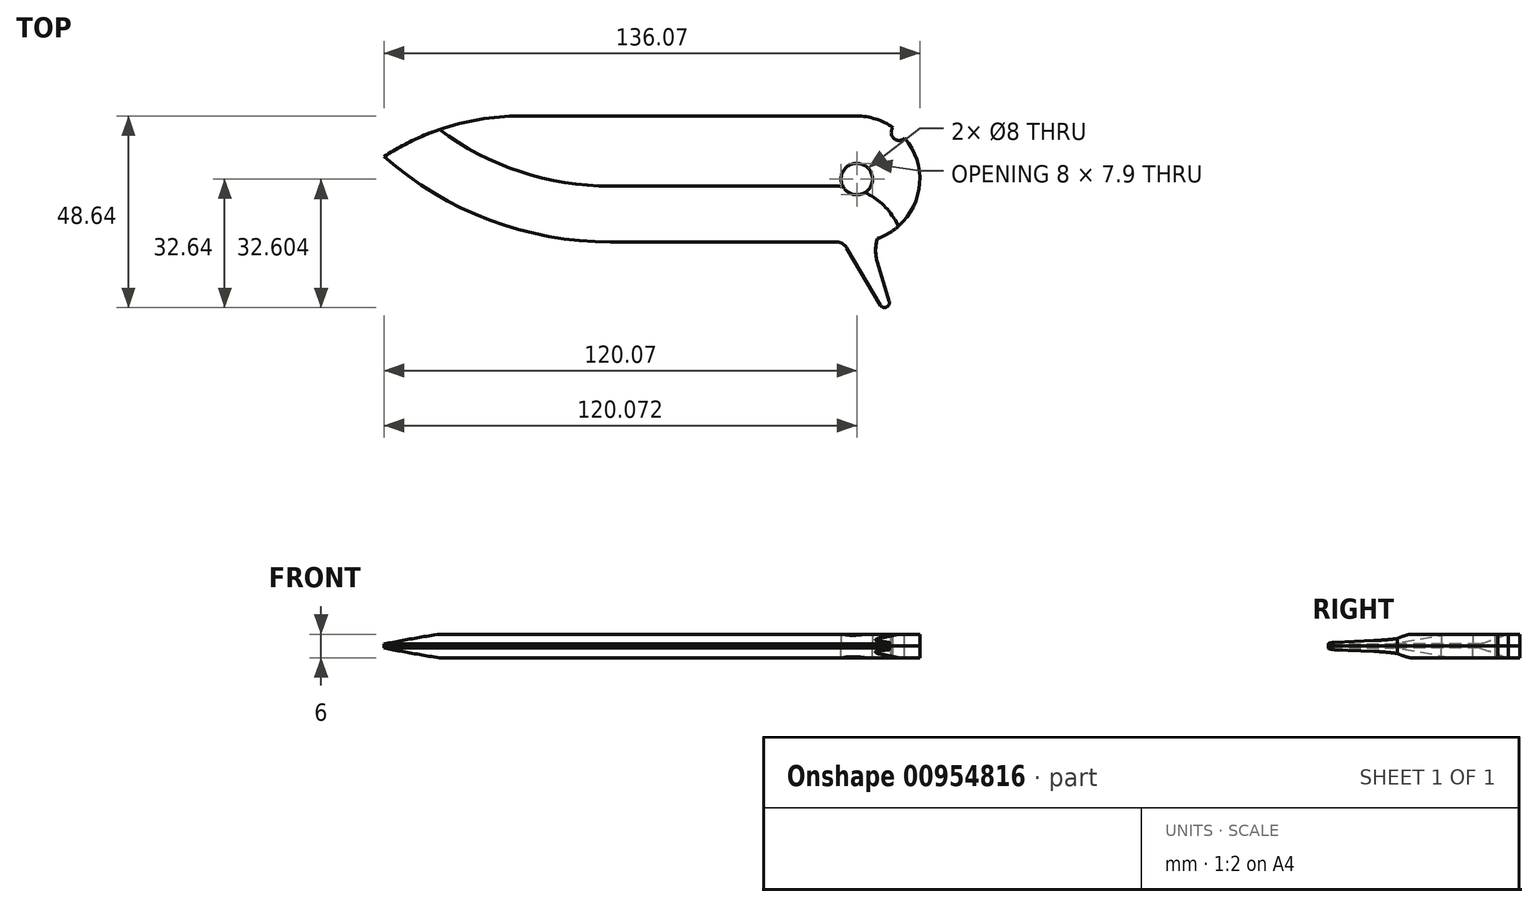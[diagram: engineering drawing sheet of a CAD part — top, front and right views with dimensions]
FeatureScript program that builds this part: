
annotation { "Feature Type Name" : "Feature", "Feature Type Description" : "" }
export const myFeature = defineFeature(function(context is Context, id is Id, definition is map)
    precondition{}
    {
        {
            var Q0;
            Q0=qCreatedBy(makeId("Top.planeOp"),FACE);
            var sketch = newSketch(context, id + "F0", { "sketchPlane" : qUnion([Q0])});
            skCircle(sketch, "E0", {"center": v(0, 0) * mm, "radius": 4 * mm});
            skArc(sketch, "E1", {"start": v(0, 16) * mm, "mid": v(15.78, 2.65) * mm, "end": v(5.24, -15.12) * mm});
            skLineSegment(sketch, "E2", {"start": v(0, 16) * mm, "end": v(-85.55, 16) * mm});
            skLineSegment(sketch, "E3", {"start": v(-62.58, -16) * mm, "end": v(-5.16, -16) * mm});
            skLineSegment(sketch, "E4", {"start": v(5.24, -21.16) * mm, "end": v(8.23, -31.02) * mm});
            skArc(sketch, "E5", {"start": v(8.23, -31.02) * mm, "mid": v(7.56, -32.53) * mm, "end": v(5.97, -32.07) * mm});
            skLineSegment(sketch, "E6", {"start": v(5.97, -32.07) * mm, "end": v(-2.57, -17.48) * mm});
            skArc(sketch, "E7.filletArc", {"start": v(-2.57, -17.48) * mm, "mid": v(-3.67, -16.4) * mm, "end": v(-5.16, -16) * mm});
            skArc(sketch, "E8", {"start": v(-85.55, 16) * mm, "mid": v(-103.56, 13.37) * mm, "end": v(-120.07, 5.7) * mm});
            skArc(sketch, "E9", {"start": v(-120.07, 5.7) * mm, "mid": v(-93.3, -10.4) * mm, "end": v(-62.58, -16) * mm});
            skPoint(sketch, "E10.orphan", {"position": v(-120, -16) * mm});
            skArc(sketch, "E11", {"start": v(5.24, -15.12) * mm, "mid": v(4.79, -18.14) * mm, "end": v(5.24, -21.16) * mm});
            skPoint(sketch, "E12.orphan", {"position": v(0, -16) * mm});
            skSolve(sketch);
        }
        {
            var Q0;
            Q0=makeQuery(id+"F0.imprint","IMPRINT",FACE,{"disambiguationData":[TD([[makeQuery(id+"F0.imprint","IMPRINT",EDGE,{"derivedFrom":sQuery(id+"F0.wireOp",EDGE,"E0")}),-1.0]])]});
            extrude(context, id + "F1", {"entities" : qUnion([Q0]), "depth" : 3 * mm, "offsetDistance" : 25 * mm});
        }
        {
            var Q0;
            Q0=makeQuery(id+"F1.opExtrude","CAP_EDGE",EDGE,{"disambiguationData":[OSD([sQuery(id+"F0.wireOp",EDGE,"E9")])],"isStart":false});
            chamfer(context, id + "F2", {"entities" : qUnion([Q0]), "chamferType" : ChamferType.OFFSET_ANGLE, "width" : 2.5 * mm, "oppositeDirection" : true, "angle" : 80 * degree, "tangentPropagation" : true});
        }
        {
            var Q0;
            Q0=makeQuery(id+"F0.imprint","IMPRINT",FACE,{"disambiguationData":[TD([[makeQuery(id+"F0.imprint","IMPRINT",EDGE,{"derivedFrom":sQuery(id+"F0.wireOp",EDGE,"E0")}),-1.0]])]});
            var sketch = newSketch(context, id + "F3", { "sketchPlane" : qUnion([Q0])});
            skArc(sketch, "E13", {"start": v(-0.13, 15.9) * mm, "mid": v(15.64, 2.55) * mm, "end": v(5.1, -15.23) * mm});
            skLineSegment(sketch, "E14", {"start": v(-0.13, 15.9) * mm, "end": v(-85.69, 15.9) * mm});
            skLineSegment(sketch, "E15", {"start": v(5.1, -21.26) * mm, "end": v(8.1, -31.13) * mm});
            skArc(sketch, "E16", {"start": v(8.1, -31.13) * mm, "mid": v(7.42, -32.63) * mm, "end": v(5.84, -32.18) * mm});
            skLineSegment(sketch, "E17", {"start": v(5.84, -32.18) * mm, "end": v(-2.7, -17.6) * mm});
            skArc(sketch, "E18", {"start": v(5.1, -15.23) * mm, "mid": v(4.65, -18.25) * mm, "end": v(5.1, -21.26) * mm});
            skLineSegment(sketch, "E19", {"start": v(-2.7, -17.6) * mm, "end": v(-10.5, -4.27) * mm});
            skLineSegment(sketch, "E20", {"start": v(-14.82, -1.8) * mm, "end": v(-25, -1.8) * mm});
            skLineSegment(sketch, "E21", {"start": v(-25, -1.8) * mm, "end": v(-25, 15.9) * mm});
            skLineSegment(sketch, "E22", {"start": v(-25, 15.9) * mm, "end": v(-0.13, 15.9) * mm});
            skPoint(sketch, "E23.visualSharp", {"position": v(-11.95, -1.8) * mm});
            skArc(sketch, "E23.filletArc", {"start": v(-10.5, -4.27) * mm, "mid": v(-12.33, -2.46) * mm, "end": v(-14.82, -1.8) * mm});
            skSolve(sketch);
        }
        {
            var Q0;
            Q0=makeQuery(id+"FeL2UTwhYUC9Mgg_0.opExtrude","SWEPT_BODY",BODY,{"disambiguationData":[OSD([sQuery(id+"F0.wireOp",EDGE,"E0"),sQuery(id+"F0.wireOp",EDGE,"E1"),sQuery(id+"F0.wireOp",EDGE,"E5"),sQuery(id+"F0.wireOp",EDGE,"E6"),sQuery(id+"F0.wireOp",EDGE,"E7.filletArc"),sQuery(id+"F0.wireOp",EDGE,"E11"),sQuery(id+"F3.wireOp",EDGE,"E13"),sQuery(id+"F3.wireOp",EDGE,"E15"),sQuery(id+"F3.wireOp",EDGE,"E16"),sQuery(id+"F3.wireOp",EDGE,"E18"),sQuery(id+"F3.wireOp",EDGE,"E19"),sQuery(id+"F3.wireOp",EDGE,"E20"),sQuery(id+"F3.wireOp",EDGE,"E21"),sQuery(id+"F3.wireOp",EDGE,"E22"),sQuery(id+"F3.wireOp",EDGE,"E23.filletArc")])]});
            var Q1;
            Q1=makeQuery(id+"F1.opExtrude","SWEPT_BODY",BODY,{"disambiguationData":[OSD([sQuery(id+"F0.wireOp",EDGE,"E0"),sQuery(id+"F0.wireOp",EDGE,"E1"),sQuery(id+"F0.wireOp",EDGE,"E2"),sQuery(id+"F0.wireOp",EDGE,"E3"),sQuery(id+"F0.wireOp",EDGE,"E4"),sQuery(id+"F0.wireOp",EDGE,"E5"),sQuery(id+"F0.wireOp",EDGE,"E6"),sQuery(id+"F0.wireOp",EDGE,"E7.filletArc"),sQuery(id+"F0.wireOp",EDGE,"E8"),sQuery(id+"F0.wireOp",EDGE,"E9"),sQuery(id+"F0.wireOp",EDGE,"E11")])]});
            var Q2;
            Q2=qCreatedBy(makeId("Top.planeOp"),FACE);
            mirror(context, id + "F4", {"entities" : qUnion([Q0, Q1]), "mirrorPlane" : qUnion([Q2])});
        }
        {
            var Q0;
            Q0=qCreatedBy(makeId("Top.planeOp"),FACE);
            var sketch = newSketch(context, id + "F5", { "sketchPlane" : qUnion([Q0])});
            skCircle(sketch, "E24", {"center": v(10.74, 11.8) * mm, "radius": 2 * mm});
            skSolve(sketch);
        }
        {
            var Q0;
            Q0 = qSketchRegion(id + "F5", true);
            extrude(context, id + "F6", {"entities" : qUnion([Q0]), "depth" : 4 * mm, "offsetDistance" : 25 * mm});
        }
        {
            var Q0;
            Q0=makeQuery(id+"F6.opExtrude","SWEPT_BODY",BODY,{"disambiguationData":[OSD([sQuery(id+"F5.wireOp",EDGE,"E24")])]});
            var Q1;
            Q1=qCreatedBy(makeId("Top.planeOp"),FACE);
            mirror(context, id + "F7", {"entities" : qUnion([Q0]), "mirrorPlane" : qUnion([Q1])});
        }
        {
            var Q0;
            Q0=makeQuery(id+"F7.opPattern","COPY",BODY,{"derivedFrom":makeQuery(id+"F6.opExtrude","SWEPT_BODY",BODY,{"disambiguationData":[OSD([sQuery(id+"F5.wireOp",EDGE,"E24")])]}),"instanceName":"1"});
            var Q1;
            Q1=makeQuery(id+"F6.opExtrude","SWEPT_BODY",BODY,{"disambiguationData":[OSD([sQuery(id+"F5.wireOp",EDGE,"E24")])]});
            var Q2;
            Q2=makeQuery(id+"FeL2UTwhYUC9Mgg_0.opExtrude","SWEPT_BODY",BODY,{"disambiguationData":[OSD([sQuery(id+"F0.wireOp",EDGE,"E0"),sQuery(id+"F0.wireOp",EDGE,"E1"),sQuery(id+"F0.wireOp",EDGE,"E5"),sQuery(id+"F0.wireOp",EDGE,"E6"),sQuery(id+"F0.wireOp",EDGE,"E7.filletArc"),sQuery(id+"F0.wireOp",EDGE,"E11"),sQuery(id+"F3.wireOp",EDGE,"E13"),sQuery(id+"F3.wireOp",EDGE,"E15"),sQuery(id+"F3.wireOp",EDGE,"E16"),sQuery(id+"F3.wireOp",EDGE,"E18"),sQuery(id+"F3.wireOp",EDGE,"E19"),sQuery(id+"F3.wireOp",EDGE,"E20"),sQuery(id+"F3.wireOp",EDGE,"E21"),sQuery(id+"F3.wireOp",EDGE,"E22"),sQuery(id+"F3.wireOp",EDGE,"E23.filletArc")])]});
            var Q3;
            Q3=makeQuery(id+"F1.opExtrude","SWEPT_BODY",BODY,{"disambiguationData":[OSD([sQuery(id+"F0.wireOp",EDGE,"E0"),sQuery(id+"F0.wireOp",EDGE,"E1"),sQuery(id+"F0.wireOp",EDGE,"E2"),sQuery(id+"F0.wireOp",EDGE,"E3"),sQuery(id+"F0.wireOp",EDGE,"E4"),sQuery(id+"F0.wireOp",EDGE,"E5"),sQuery(id+"F0.wireOp",EDGE,"E6"),sQuery(id+"F0.wireOp",EDGE,"E7.filletArc"),sQuery(id+"F0.wireOp",EDGE,"E8"),sQuery(id+"F0.wireOp",EDGE,"E9"),sQuery(id+"F0.wireOp",EDGE,"E11")])]});
            var Q4;
            Q4=makeQuery(id+"F4.opPattern","COPY",BODY,{"derivedFrom":makeQuery(id+"F1.opExtrude","SWEPT_BODY",BODY,{"disambiguationData":[OSD([sQuery(id+"F0.wireOp",EDGE,"E0"),sQuery(id+"F0.wireOp",EDGE,"E1"),sQuery(id+"F0.wireOp",EDGE,"E2"),sQuery(id+"F0.wireOp",EDGE,"E3"),sQuery(id+"F0.wireOp",EDGE,"E4"),sQuery(id+"F0.wireOp",EDGE,"E5"),sQuery(id+"F0.wireOp",EDGE,"E6"),sQuery(id+"F0.wireOp",EDGE,"E7.filletArc"),sQuery(id+"F0.wireOp",EDGE,"E8"),sQuery(id+"F0.wireOp",EDGE,"E9"),sQuery(id+"F0.wireOp",EDGE,"E11")])]}),"instanceName":"1"});
            booleanBodies(context, id + "F8", {"operationType" : BooleanOperationType.SUBTRACTION, "tools" : qUnion([Q0, Q1]), "targets" : qUnion([Q2, Q3, Q4])});
        }
    });
